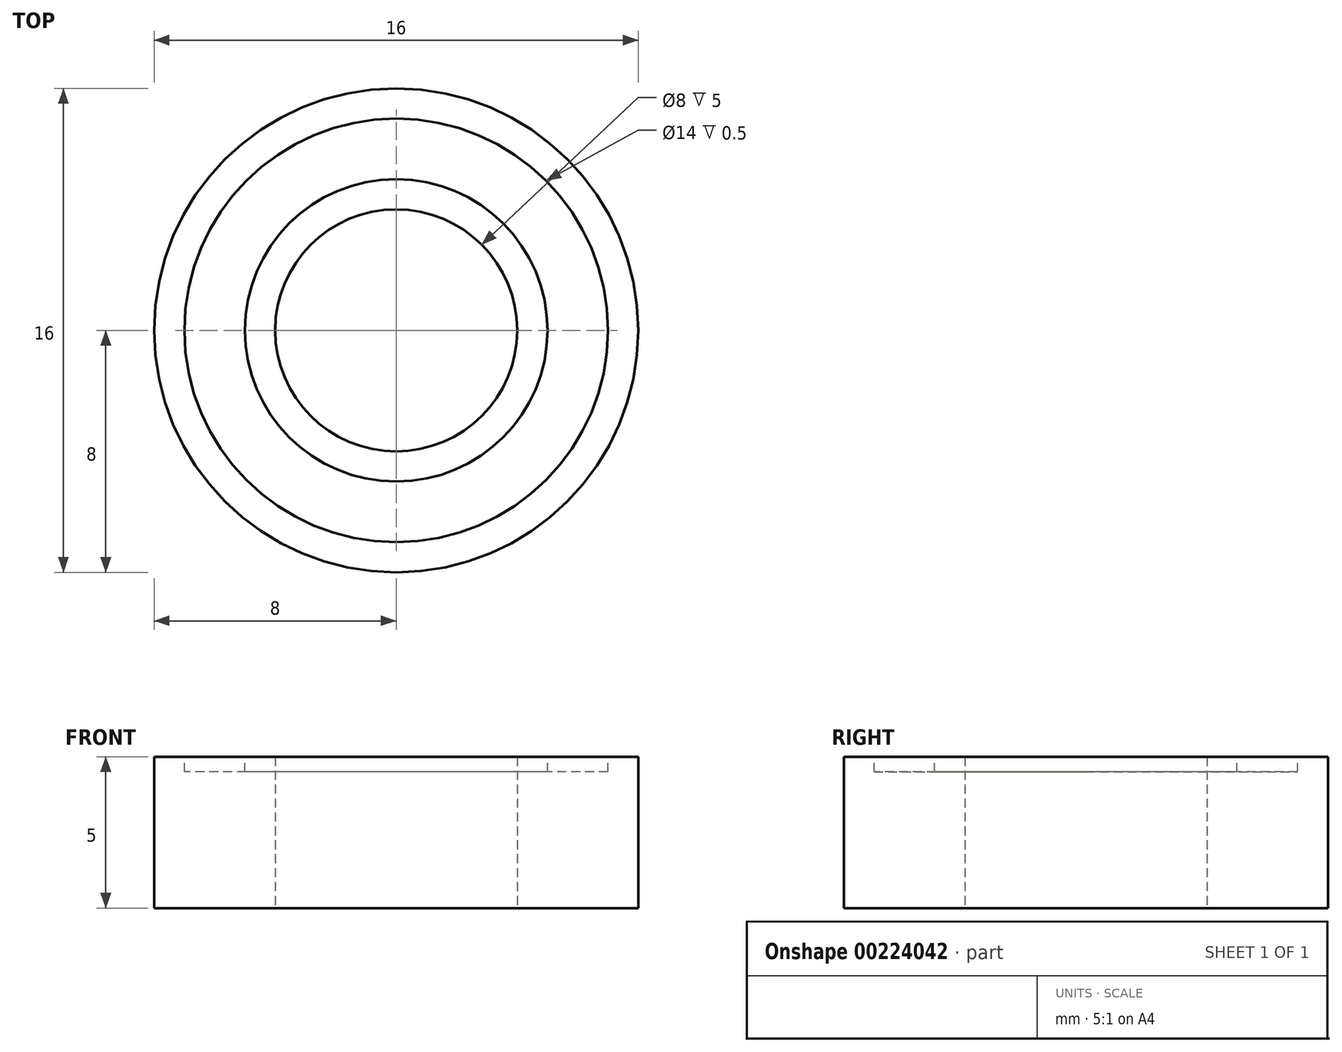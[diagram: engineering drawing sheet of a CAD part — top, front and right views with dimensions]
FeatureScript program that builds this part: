
annotation { "Feature Type Name" : "Feature", "Feature Type Description" : "" }
export const myFeature = defineFeature(function(context is Context, id is Id, definition is map)
    precondition{}
    {
        {
            var Q0;
            Q0=qCreatedBy(makeId("Top.planeOp"),FACE);
            var sketch = newSketch(context, id + "F0", { "sketchPlane" : qUnion([Q0])});
            skCircle(sketch, "E0", {"center": v(0, 0) * mm, "radius": 8 * mm});
            skCircle(sketch, "E1", {"center": v(0, 0) * mm, "radius": 4 * mm});
            skSolve(sketch);
        }
        {
            var Q0;
            Q0 = qSketchRegion(id + "F0", true);
            extrude(context, id + "F1", {"entities" : qUnion([Q0]), "depth" : 5 * mm});
        }
        {
            var Q0;
            Q0=makeQuery(id+"F1.opExtrude","CAP_FACE",FACE,{"disambiguationData":[OSD([sQuery(id+"F0.wireOp",EDGE,"E0"),sQuery(id+"F0.wireOp",EDGE,"E1")])],"isStart":false});
            var sketch = newSketch(context, id + "F2", { "sketchPlane" : qUnion([Q0])});
            skCircle(sketch, "E2", {"center": v(0, 0) * mm, "radius": 5 * mm});
            skCircle(sketch, "E3", {"center": v(0, 0) * mm, "radius": 7 * mm});
            skSolve(sketch);
        }
        {
            var Q0;
            Q0=makeQuery(id+"F2.imprint","IMPRINT",FACE,{"disambiguationData":[TD([[makeQuery(id+"F2.imprint","IMPRINT",EDGE,{"derivedFrom":sQuery(id+"F2.wireOp",EDGE,"E2")}),-1.0]])]});
            extrude(context, id + "F3", {"entities" : qUnion([Q0]), "operationType" : NewBodyOperationType.REMOVE, "oppositeDirection" : true, "depth" : .5 * mm});
        }
    });
